# Revit family: Geräteeinsätze GES_Geräteeinsatz_Revisionsabdeckung ZESRA7
name_source: partatom
category: Generic Models
revit_build: Autodesk Revit 2015 (Build: 20140606_1530(x64)
units: mm (PartAtom-declared; Revit-internal decimal feet)

## types (1)
- ZESRA7 10U
    Article Type = ZESRA7 10U
    Bodenbelagdicke = 10 mm  [stored 0.0328084 ft]
    Diameter dimesion = 274 mm  [stored 0.89895 ft]
    GTIN = 4012195109730
    Height = 35 mm  [stored 0.114829 ft]
    Inner cut = 266 mm  [stored 0.872703 ft]
    Inner cut 3 = 165 mm
    Inner cut2 = 230 mm  [stored 0.754593 ft]
    Manufacturer = OBO Bettermann
    Manufacturer Art. No. = 7406824
    Material = Aluminum 6061
    Outer Diameter Dimension = 294 mm  [stored 0.964567 ft]
    URL = http://www.obo-bettermann.com

note: [stored X ft] marks values corroborated as IEEE doubles in the binary element streams (Revit-internal decimal feet)

## geometry (parser evidence)
native form markers: Sweep x2
no freeform markers — native parametric forms only
